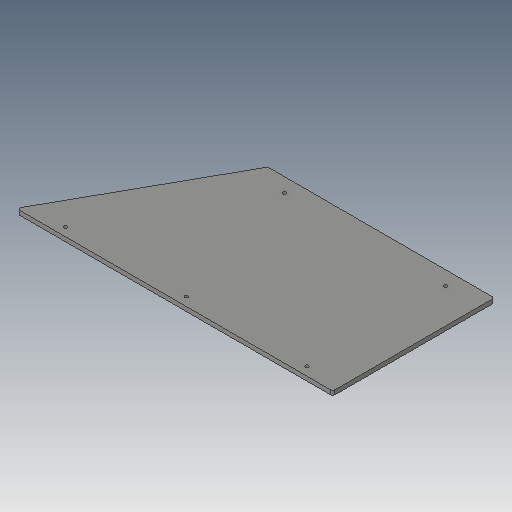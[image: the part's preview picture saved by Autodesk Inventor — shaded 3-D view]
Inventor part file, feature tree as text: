
AUTODESK INVENTOR PART (.ipt)
format: ipt  version: 2023.5 (Build 275446000, 446)  size: 91,136 bytes
history: native  units: in
note: dims shown in document units (in); Inventor stores cm internally (conversion verified against a paired STEP export)
features: fillet x1
ambient origin geometry x8: Origin, YZ Plane, XZ Plane, XY Plane, X Axis, Y Axis, Z Axis, Center Point
bodies: Solid1 (feature_tree)
feature tree (1):
  fillet  "Fillet1"  [1 undecoded]
note: 1 required parameter value undecoded (feature->parameter linkage not recoverable at this tier; creation-order binding heuristic only, values carry confidence <= 0.55)
